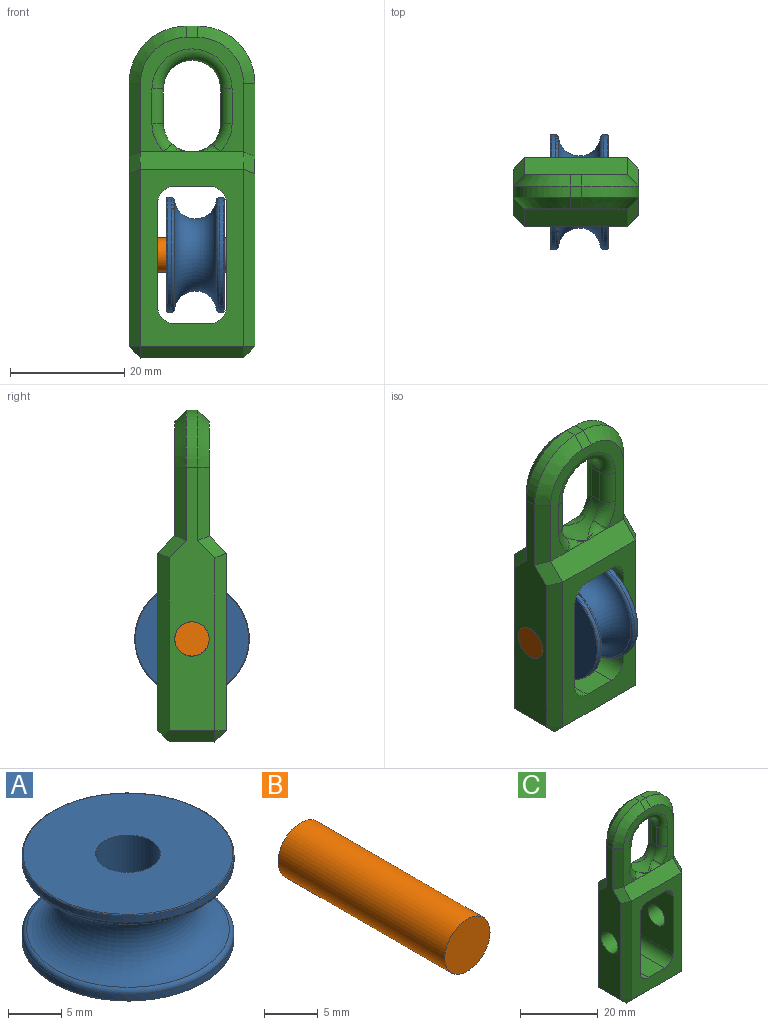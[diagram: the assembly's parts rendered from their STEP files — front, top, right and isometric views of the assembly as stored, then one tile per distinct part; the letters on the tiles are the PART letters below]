
ASSEMBLY  parts=3 mates=3
PART A: 10 faces, bbox 21.6x21.6x10 mm
  f0: plane 19.8x19.8mm, normal (0,0,1), area 278.7mm2, adj f1,f8
  f1: cylinder r=3.05mm len=10mm, axis (0,0,-1), area 191.6mm2, adj f0,f2
  f2: plane 19.8x19.8mm, normal (0,0,-1), area 278.7mm2, adj f1,f9
  f3: cylinder r=10mm len=20mm, axis (0,0,-1), area 45.9mm2, adj f7,f9
  f4: torus R=10mm, axis (0,0,-1), area 504.1mm2, adj f6,f7
  f5: cylinder r=10mm len=20mm, axis (0,0,-1), area 45.9mm2, adj f6,f8
  f6: torus R=9.5mm, axis (0,0,1), area 44.9mm2, adj f4,f5
  f7: torus R=9.5mm, axis (0,0,1), area 44.9mm2, adj f3,f4
  f8: torus R=9.9mm, axis (0,0,1), area 9.8mm2, adj f0,f5
  f9: torus R=9.9mm, axis (0,0,-1), area 9.8mm2, adj f2,f3
PART B: 3 faces, bbox 6x22x6 mm
  f0: cylinder r=2.99mm len=22mm, axis (0,-1,0), area 413.3mm2, adj f1,f2
  f1: plane 5.98x5.98mm, normal (0,-1,0), area 28.1mm2, adj f0
  f2: plane 5.98x5.98mm, normal (0,1,0), area 28.1mm2, adj f0
PART C: 64 faces, bbox 22.2x12.2x58.2 mm
  f0: plane 46x8mm, normal (-1,0,0), area 253.8mm2, adj f6,f25,f27,f29,f42,f44,f45,f47
  f1: plane 46x8mm, normal (1,0,0), area 253.8mm2, adj f4,f30,f32,f33,f34,f36,f38,f39
  f2: plane 18x12mm, normal (-1,0,0), area 187.7mm2, adj f7,f13,f16,f17,f63
  f3: plane 18x12mm, normal (1,0,0), area 187.7mm2, adj f7,f13,f14,f19,f62
  f4: cylinder r=10mm len=10mm, axis (0,1,0), area 31.4mm2, adj f1,f5,f28,f35
  f5: plane 2x2mm, normal (0,0,1), area 4mm2, adj f4,f6,f26,f37
  f6: cylinder r=10mm len=10mm, axis (0,1,0), area 31.4mm2, adj f0,f5,f24,f40
  f7: plane 31x18mm, normal (0,-1,0), area 277.7mm2, adj f2,f3,f14,f15,f16,f17,f18,f19
  f8: cylinder r=5mm len=10mm, axis (0,-1,0), area 43.3mm2, adj f9,f11,f48,f49,f53,f54,f55,f56
  f9: plane 6x2mm, normal (1,0,0), area 12mm2, adj f8,f10,f52,f57
  f10: cylinder r=5mm len=10mm, axis (0,-1,0), area 31.4mm2, adj f9,f11,f51,f58
  f11: plane 6x2mm, normal (-1,0,0), area 12mm2, adj f8,f10,f50,f59
  f12: plane 18x8mm, normal (0,0,-1), area 144mm2, adj f31,f39,f43,f44
  f13: plane 31x18mm, normal (0,1,0), area 277.7mm2, adj f2,f3,f14,f15,f16,f17,f18,f19
  f14: cylinder r=3mm len=12mm, axis (0,-1,0), area 56.5mm2, adj f3,f7,f13,f15
  f15: plane 12x6mm, normal (0,0,-1), area 72mm2, adj f7,f13,f14,f16
  f16: cylinder r=3mm len=12mm, axis (0,-1,0), area 56.5mm2, adj f2,f7,f13,f15
  f17: cylinder r=3mm len=12mm, axis (0,-1,0), area 56.5mm2, adj f2,f7,f13,f18
  f18: plane 12x6mm, normal (0,0,1), area 72mm2, adj f7,f13,f17,f19
  f19: cylinder r=3mm len=12mm, axis (0,-1,0), area 56.5mm2, adj f3,f7,f13,f18
  f20: plane 20x18mm, normal (0,-1,0), area 108.1mm2, adj f22,f34,f35,f37,f40,f42,f49,f50
  f21: plane 20x18mm, normal (0,1,0), area 108.1mm2, adj f23,f24,f25,f26,f28,f30,f56,f57
  f22: plane 18.21x3.21mm, normal (0,-0.71,0.71), area 76.4mm2, adj f7,f20,f36,f45,f48,f54
  f23: plane 18.21x3.21mm, normal (0,0.71,0.71), area 76.4mm2, adj f13,f21,f27,f32,f55,f60
  f24: cone r=10mm half-angle=45deg, axis (0,-1,0), area 40mm2, adj f6,f21,f25,f26
  f25: plane 12.83x2mm, normal (-0.71,0.71,0), area 35.1mm2, adj f0,f21,f24,f27
  f26: plane 2x2mm, normal (0,0.71,0.71), area 5.7mm2, adj f5,f21,f24,f28
  f27: plane 5x3.83mm, normal (-0.71,0.5,0.5), area 12mm2, adj f0,f23,f25,f29
  f28: cone r=10mm half-angle=45deg, axis (0,-1,0), area 40mm2, adj f4,f21,f26,f30
  f29: plane 32x2mm, normal (-0.71,0.71,0), area 87.9mm2, adj f0,f13,f27,f31,f44
  f30: plane 12.83x2mm, normal (0.71,0.71,0), area 35.1mm2, adj f1,f21,f28,f32
  f31: plane 20x2mm, normal (0,0.71,-0.71), area 53.7mm2, adj f12,f13,f29,f33,f39,f44
  f32: plane 5x3.83mm, normal (0.71,0.5,0.5), area 12mm2, adj f1,f23,f30,f33
  f33: plane 32x2mm, normal (0.71,0.71,0), area 87.9mm2, adj f1,f13,f31,f32,f39
  f34: plane 12.83x2mm, normal (0.71,-0.71,0), area 35.1mm2, adj f1,f20,f35,f36
  f35: cone r=8mm half-angle=45deg, axis (0,1,0), area 40mm2, adj f4,f20,f34,f37
  f36: plane 5x3.83mm, normal (0.71,-0.5,0.5), area 12mm2, adj f1,f22,f34,f38
  f37: plane 2x2mm, normal (0,-0.71,0.71), area 5.7mm2, adj f5,f20,f35,f40
  f38: plane 31x2mm, normal (0.71,-0.71,0), area 86.5mm2, adj f1,f7,f36,f41
  f39: plane 9x2mm, normal (0.71,0,-0.71), area 24mm2, adj f1,f12,f31,f33,f41
  f40: cone r=8mm half-angle=45deg, axis (0,1,0), area 40mm2, adj f6,f20,f37,f42
  f41: plane 2x2mm, normal (0.58,-0.58,-0.58), area 3.5mm2, adj f38,f39,f43
  f42: plane 12.83x2mm, normal (-0.71,-0.71,0), area 35.1mm2, adj f0,f20,f40,f45
  f43: plane 18x2mm, normal (0,-0.71,-0.71), area 50.9mm2, adj f7,f12,f41,f46
  f44: plane 9x2mm, normal (-0.71,0,-0.71), area 24mm2, adj f0,f12,f29,f31,f46
  f45: plane 5x3.83mm, normal (-0.71,-0.5,0.5), area 12mm2, adj f0,f22,f42,f47
  f46: plane 2x2mm, normal (-0.58,-0.58,-0.58), area 3.5mm2, adj f43,f44,f47
  f47: plane 31x2mm, normal (-0.71,-0.71,0), area 86.5mm2, adj f0,f7,f45,f46
  f48: bspline ~5.05x2.1mm, area 6.1mm2, adj f8,f22,f49
  f49: torus R=7mm, axis (0,-1,0), area 14.3mm2, adj f8,f20,f48,f50
  f50: cylinder r=2mm len=6mm, axis (0,0,1), area 18.8mm2, adj f11,f20,f49,f51
  f51: torus R=7mm, axis (0,-1,0), area 56.5mm2, adj f10,f20,f50,f52
  f52: cylinder r=2mm len=6mm, axis (0,0,-1), area 18.8mm2, adj f9,f20,f51,f53
  f53: torus R=7mm, axis (0,-1,0), area 14.3mm2, adj f8,f20,f52,f54
  f54: bspline ~5.05x2.1mm, area 6.1mm2, adj f8,f22,f53
  f55: bspline ~5.05x2.1mm, area 6.1mm2, adj f8,f23,f56
  f56: torus R=7mm, axis (0,-1,0), area 14.3mm2, adj f8,f21,f55,f57
  f57: cylinder r=2mm len=6mm, axis (0,0,1), area 18.8mm2, adj f9,f21,f56,f58
  f58: torus R=7mm, axis (0,-1,0), area 56.5mm2, adj f10,f21,f57,f59
  f59: cylinder r=2mm len=6mm, axis (0,0,-1), area 18.8mm2, adj f11,f21,f58,f61
  f60: bspline ~5.05x2.1mm, area 6.1mm2, adj f8,f23,f61
  f61: torus R=7mm, axis (0,-1,0), area 14.3mm2, adj f8,f21,f59,f60
  f62: cylinder r=3mm len=6mm, axis (-1,0,0), area 94.2mm2, adj f0,f3
  f63: cylinder r=3mm len=6mm, axis (-1,0,0), area 94.2mm2, adj f1,f2
PLACE A rot(axis=(0.68,-0.26,-0.68),150.6deg) t=(0.71,-0.25,-9.53)mm
PLACE B rot(axis=(0,0,-1),90deg) t=(-10.89,-6.24,-27.53)mm
PLACE C rot(axis=(1,0,0),0deg) t=(-10.89,5.76,-27.52)mm fixed
MATE fastened B.f0 <-> C.f62  axis (-1,0,0) through (-10.89,-0.25,-9.53)mm
MATE cylindrical C.f62 <-> B.f0  axis (-1,0,0) through (-10.89,-0.25,-9.53)mm
MATE cylindrical B.f0 <-> A.f1  axis (-1,0,0) through (0.11,-0.25,-9.53)mm
